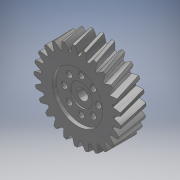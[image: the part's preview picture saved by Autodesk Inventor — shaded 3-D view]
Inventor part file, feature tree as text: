
AUTODESK INVENTOR PART (.ipt)
format: ipt  version: 2019 (Build 230136000, 136)  size: 578,048 bytes
history: native  units: mm (DEFAULTED — no unit token found)
features: sketch x10, extrude x7, plane x3, other x3, hole x2, chamfer x1
ambient origin geometry x8: Origin, YZ Plane, XZ Plane, XY Plane, X Axis, Y Axis, Z Axis, Center Point
bodies: Solid1 (feature_tree)
feature tree (26):
  extrude  "Extrusion1"  Depth=10.0mm TaperAngle=0.0deg
  plane  "Work Plane2"
  plane  "Work Plane8"
  plane  "Work Plane9"
  other  "Spur Gear"
  hole  "Hole1"  [1 undecoded]
  extrude  "Extrusion4"  Depth=1.256637mm TaperAngle=0.0deg
  extrude  "Extrusion6"  TaperAngle=0.0deg  [1 undecoded]
  hole  "Hole3"  [1 undecoded]
  extrude  "Extrusion8"  Depth=8.0mm
  chamfer  "Chamfer1"  Distance=1.5mm
  extrude  "Extrusion9"  Depth=9.0mm
  extrude  "Extrusion10"  Depth=13.5mm
  extrude  "Extrusion12"  Depth=0.5mm TaperAngle=0.0deg
  sketch  "Sketch1"  dims[d0=34.756617mm d1=10.0mm d2=0.0mm]
  sketch  "Sketch2"  dims[d3=32.258065mm d4=10.0mm d5=0.0mm]
  other  "Srf1"
  sketch  "Sketch5"  dims[d16=40.0mm d17=0.0mm d34=1.256637mm]
  sketch  "Sketch6"  dims[d39=0.0mm d41=0.0mm]
  sketch  "Sketch10"  dims[d43=40.0mm d46=40.0mm]
  sketch  "Sketch11"  dims[d47=0.0mm d48=0.0mm]
  sketch  "Sketch14"  dims[d55=4.5mm d56=6.0mm d57=6.5mm d58=4.0mm d59=90.0deg d60=8.0mm d61=20.594885mm d62=20.0mm d63=1.5mm d64=0.0mm]
  sketch  "Sketch15"  dims[d82=18.0mm d83=9.0mm]
  sketch  "Sketch16"  dims[d84=5.0mm d85=0.0mm d86=13.5mm]
  sketch  "Sketch18"  dims[d87=80.0mm d89=360.0deg d91=2.5mm d92=6.0mm d93=4.0mm d94=3.0mm d95=90.0deg d96=8.0mm d97=20.594885mm d100=5.0mm d101=0.0mm d102=1.5mm d103=4.0mm d104=12.217305mm d105=9.0mm d106=0.5mm d107=0.0mm d108=80.0mm d110=360.0deg d112=0.3mm d113=0.0mm d120=80.0mm d122=360.0deg d124=0.3mm d125=0.0mm]
  other  "Pitch Diameter"
note: 3 required parameter values undecoded (feature->parameter linkage not recoverable at this tier; creation-order binding heuristic only, values carry confidence <= 0.55)
